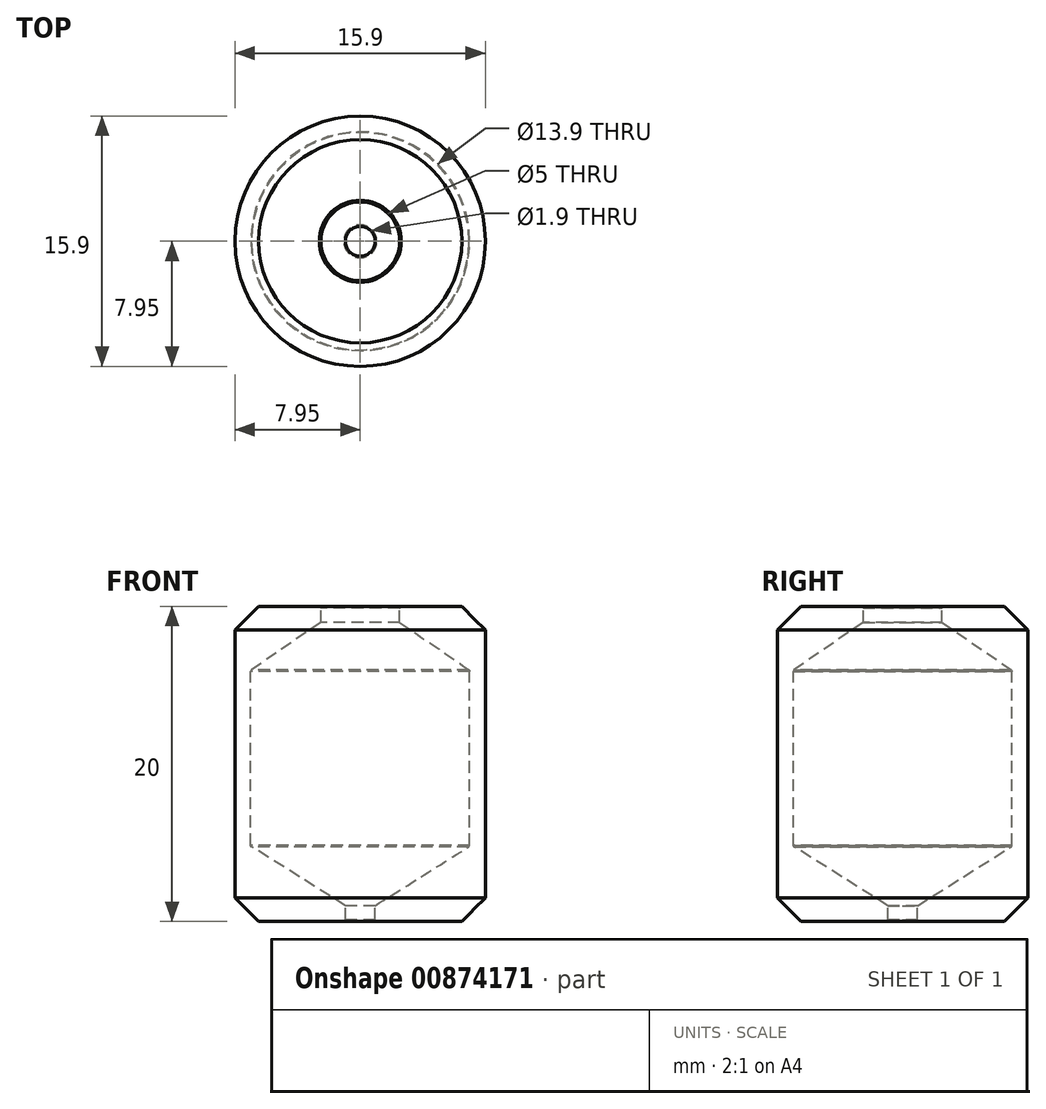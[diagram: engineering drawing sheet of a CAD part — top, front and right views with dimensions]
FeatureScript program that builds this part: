
annotation { "Feature Type Name" : "Feature", "Feature Type Description" : "" }
export const myFeature = defineFeature(function(context is Context, id is Id, definition is map)
    precondition{}
    {
        {
            var Q0;
            Q0=qCreatedBy(makeId("Front.planeOp"),FACE);
            var sketch = newSketch(context, id + "F0", { "sketchPlane" : qUnion([Q0])});
            skLineSegment(sketch, "E0", {"start": v(0, 0) * mm, "end": v(-0.95, 0) * mm});
            skLineSegment(sketch, "E1", {"start": v(-0.95, 0) * mm, "end": v(-7.95, 0) * mm});
            skLineSegment(sketch, "E2", {"start": v(-7.95, 0) * mm, "end": v(-7.95, 20) * mm});
            skLineSegment(sketch, "E3", {"start": v(0, 20) * mm, "end": v(-2.5, 20) * mm});
            skLineSegment(sketch, "E4", {"start": v(-2.5, 20) * mm, "end": v(-7.95, 20) * mm});
            skLineSegment(sketch, "E5.0", {"start": v(-0.95, 1) * mm, "end": v(-6.95, 1) * mm});
            skLineSegment(sketch, "E5.1", {"start": v(-6.95, 1) * mm, "end": v(-6.95, 19) * mm});
            skLineSegment(sketch, "E5.2", {"start": v(-2.5, 19) * mm, "end": v(-6.95, 19) * mm});
            skLineSegment(sketch, "E6", {"start": v(-2.5, 19) * mm, "end": v(-2.5, 20) * mm});
            skLineSegment(sketch, "E7", {"start": v(-0.95, 0) * mm, "end": v(-0.95, 1) * mm});
            skLineSegment(sketch, "E8", {"start": v(0, 20) * mm, "end": v(0, 0) * mm});
            skLineSegment(sketch, "E9", {"start": v(-2.5, 19) * mm, "end": v(-6.95, 15.94) * mm});
            skLineSegment(sketch, "E10", {"start": v(-0.95, 1) * mm, "end": v(-6.95, 4.77) * mm});
            skSolve(sketch);
        }
        {
            var Q0;
            Q0=makeQuery(id+"F0.imprint","IMPRINT",FACE,{"disambiguationData":[TD([[makeQuery(id+"F0.imprint","IMPRINT",EDGE,{"derivedFrom":sQuery(id+"F0.wireOp",EDGE,"E1")}),-1.0]])]});
            var Q1;
            {var subQ0=sQuery(id+"F0.wireOp",EDGE,"E5.2");Q1=makeQuery(id+"F0.imprint","IMPRINT",FACE,{"disambiguationData":[TD([[makeQuery(id+"F0.imprint","IMPRINT",EDGE,{"derivedFrom":subQ0}),1.0]])]});}
            var Q2;
            {var subQ0=sQuery(id+"F0.wireOp",EDGE,"E5.0");Q2=makeQuery(id+"F0.imprint","IMPRINT",FACE,{"disambiguationData":[TD([[makeQuery(id+"F0.imprint","IMPRINT",EDGE,{"derivedFrom":subQ0}),-1.0]])]});}
            var Q3;
            Q3=sQuery(id+"F0.wireOp",EDGE,"E8");
            revolve(context, id + "F1", {"surfaceOperationType" : NewSurfaceOperationType.NEW, "entities" : qUnion([Q0, Q1, Q2]), "axis" : qUnion([Q3]), "revolveType" : RevolveType.FULL});
        }
        {
            var Q0;
            Q0=makeQuery(id+"F1.opRevolve","SWEPT_EDGE",EDGE,{"disambiguationData":[OSD([sQuery(id+"F0.wireOp",EDGE,"E2"),sQuery(id+"F0.wireOp",EDGE,"E4")])]});
            var Q1;
            Q1=makeQuery(id+"F1.opRevolve","SWEPT_EDGE",EDGE,{"disambiguationData":[OSD([sQuery(id+"F0.wireOp",EDGE,"E1"),sQuery(id+"F0.wireOp",EDGE,"E2")])]});
            chamfer(context, id + "F2", {"entities" : qUnion([Q0, Q1]), "width" : 1.5 * mm, "tangentPropagation" : true});
        }
        {
            var Q0;
            Q0=makeQuery(id+"F1.opRevolve","SWEPT_EDGE",EDGE,{"disambiguationData":[OSD([sQuery(id+"F0.wireOp",EDGE,"E5.1"),sQuery(id+"F0.wireOp",EDGE,"E10")])]});
            var Q1;
            Q1=makeQuery(id+"F1.opRevolve","SWEPT_EDGE",EDGE,{"disambiguationData":[OSD([sQuery(id+"F0.wireOp",EDGE,"E5.1"),sQuery(id+"F0.wireOp",EDGE,"E9")])]});
            var Q2;
            Q2=makeQuery(id+"F1.opRevolve","SWEPT_EDGE",EDGE,{"disambiguationData":[OSD([sQuery(id+"F0.wireOp",EDGE,"E0"),sQuery(id+"F0.wireOp",EDGE,"E1"),sQuery(id+"F0.wireOp",EDGE,"E7")])]});
            var Q3;
            Q3=makeQuery(id+"F1.opRevolve","SWEPT_EDGE",EDGE,{"disambiguationData":[OSD([sQuery(id+"F0.wireOp",EDGE,"E3"),sQuery(id+"F0.wireOp",EDGE,"E4"),sQuery(id+"F0.wireOp",EDGE,"E6")])]});
            chamfer(context, id + "F3", {"entities" : qUnion([Q0, Q1, Q2, Q3]), "width" : .1 * mm, "tangentPropagation" : true});
        }
    });
